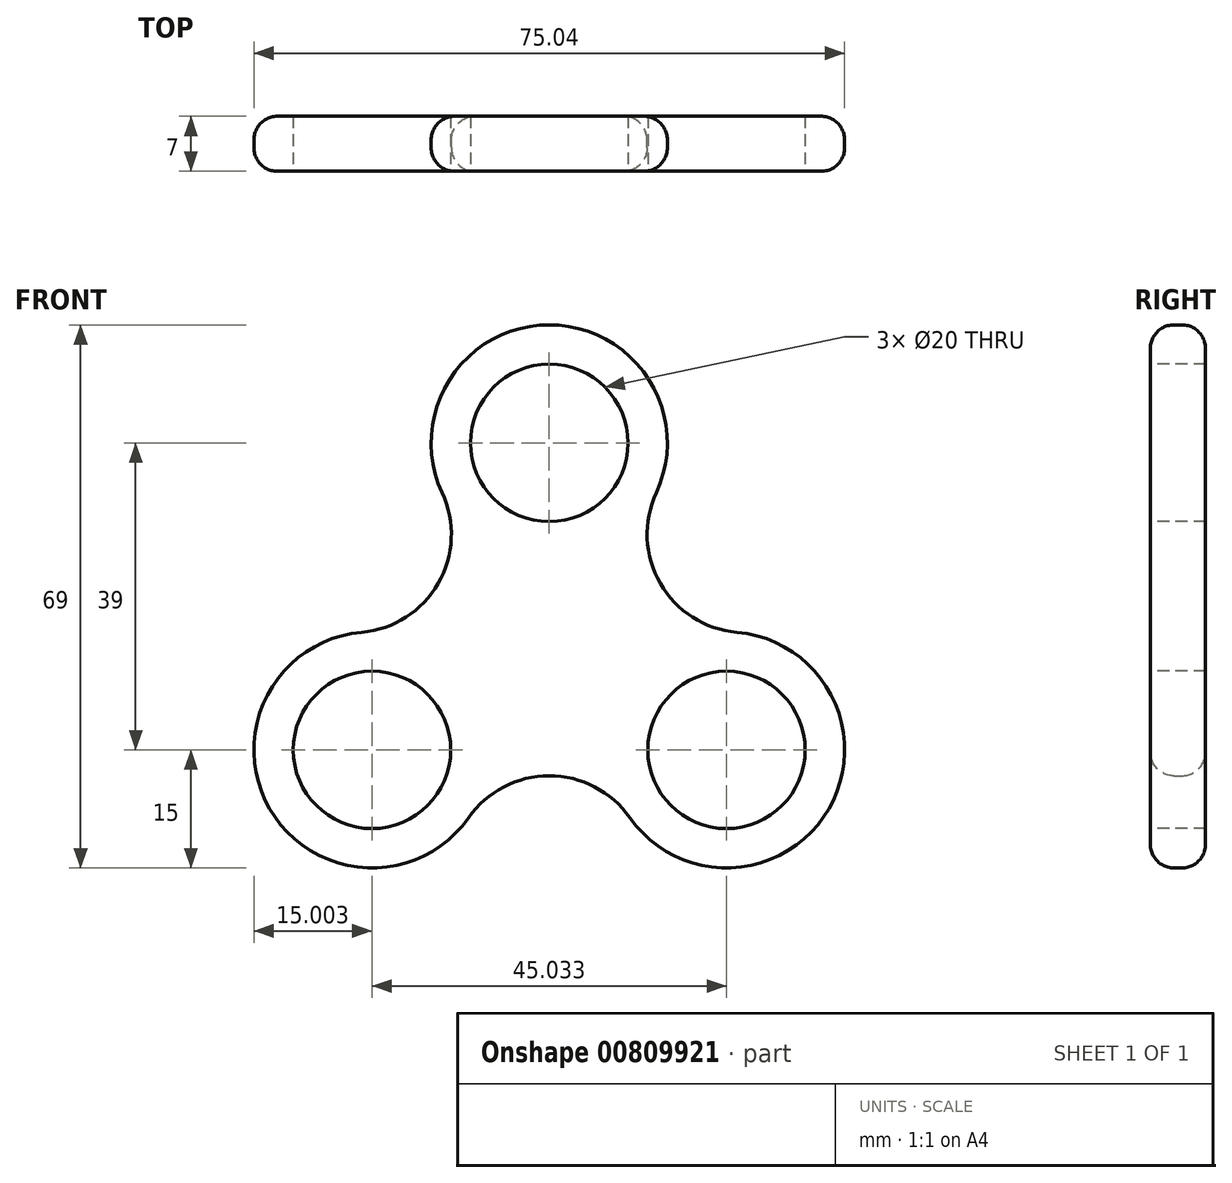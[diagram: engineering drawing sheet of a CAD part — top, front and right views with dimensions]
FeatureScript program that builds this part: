
annotation { "Feature Type Name" : "Feature", "Feature Type Description" : "" }
export const myFeature = defineFeature(function(context is Context, id is Id, definition is map)
    precondition{}
    {
        {
            var Q0;
            Q0=qCreatedBy(makeId("Front.planeOp"),FACE);
            var sketch = newSketch(context, id + "F0", { "sketchPlane" : qUnion([Q0])});
            skCircle(sketch, "E0", {"center": v(0, 26) * mm, "radius": 15 * mm});
            skCircle(sketch, "E1", {"center": v(-22.52, -13) * mm, "radius": 15 * mm});
            skCircle(sketch, "E2", {"center": v(22.52, -13) * mm, "radius": 15 * mm});
            skCircle(sketch, "E3", {"center": v(0, 0) * mm, "radius": 26 * mm, "construction": true});
            skLineSegment(sketch, "E4", {"start": v(0, 0) * mm, "end": v(-56.23, -32.46) * mm, "construction": true});
            skLineSegment(sketch, "E5", {"start": v(0, 0) * mm, "end": v(54.96, -31.73) * mm, "construction": true});
            skArc(sketch, "E6", {"start": v(-23.83, 1.94) * mm, "mid": v(-14.1, 8.14) * mm, "end": v(-13.6, 19.67) * mm});
            skArc(sketch, "E7", {"start": v(10.23, -21.61) * mm, "mid": v(0, -16.29) * mm, "end": v(-10.23, -21.61) * mm});
            skArc(sketch, "E8", {"start": v(13.6, 19.67) * mm, "mid": v(14.1, 8.14) * mm, "end": v(23.83, 1.94) * mm});
            skSolve(sketch);
        }
        {
            var Q0;
            {var subQ0=sQuery(id+"F0.wireOp",EDGE,"E0");var subQ1=makeQuery(id+"F0.imprint","INTERSECT",VERTEX,{"derivedFrom":[subQ0,sQuery(id+"F0.wireOp",EDGE,"E6")]});Q0=makeQuery(id+"F0.imprint","IMPRINT",FACE,{"disambiguationData":[TD([[makeQuery(id+"F0.imprint","IMPRINT",EDGE,{"disambiguationData":[TD([[subQ1,-1.0]])],"derivedFrom":subQ0}),1.0]])]});}
            var Q1;
            {var subQ0=sQuery(id+"F0.wireOp",EDGE,"E1");var subQ1=makeQuery(id+"F0.imprint","INTERSECT",VERTEX,{"derivedFrom":[subQ0,sQuery(id+"F0.wireOp",EDGE,"E6")]});Q1=makeQuery(id+"F0.imprint","IMPRINT",FACE,{"disambiguationData":[TD([[makeQuery(id+"F0.imprint","IMPRINT",EDGE,{"disambiguationData":[TD([[subQ1,-1.0]])],"derivedFrom":subQ0}),1.0]])]});}
            var Q2;
            {var subQ0=sQuery(id+"F0.wireOp",EDGE,"E2");var subQ1=makeQuery(id+"F0.imprint","INTERSECT",VERTEX,{"derivedFrom":[subQ0,sQuery(id+"F0.wireOp",EDGE,"E7")]});Q2=makeQuery(id+"F0.imprint","IMPRINT",FACE,{"disambiguationData":[TD([[makeQuery(id+"F0.imprint","IMPRINT",EDGE,{"disambiguationData":[TD([[subQ1,1.0]])],"derivedFrom":subQ0}),1.0]])]});}
            var Q3;
            {var subQ0=sQuery(id+"F0.wireOp",EDGE,"E6");Q3=makeQuery(id+"F0.imprint","IMPRINT",FACE,{"disambiguationData":[TD([[makeQuery(id+"F0.imprint","IMPRINT",EDGE,{"derivedFrom":subQ0}),-1.0]])]});}
            extrude(context, id + "F1", {"entities" : qUnion([Q0, Q1, Q2, Q3]), "depth" : 7 * mm, "offsetDistance" : 25 * mm, "symmetric" : true});
        }
        {
            var Q0;
            Q0=makeQuery(id+"F1.opExtrude","CAP_FACE",FACE,{"disambiguationData":[OSD([sQuery(id+"F0.wireOp",EDGE,"E0"),sQuery(id+"F0.wireOp",EDGE,"E1"),sQuery(id+"F0.wireOp",EDGE,"E2"),sQuery(id+"F0.wireOp",EDGE,"E6"),sQuery(id+"F0.wireOp",EDGE,"E7"),sQuery(id+"F0.wireOp",EDGE,"E8")])],"isStart":false});
            var Q1;
            Q1=makeQuery(id+"F1.opExtrude","CAP_FACE",FACE,{"disambiguationData":[OSD([sQuery(id+"F0.wireOp",EDGE,"E0"),sQuery(id+"F0.wireOp",EDGE,"E1"),sQuery(id+"F0.wireOp",EDGE,"E2"),sQuery(id+"F0.wireOp",EDGE,"E6"),sQuery(id+"F0.wireOp",EDGE,"E7"),sQuery(id+"F0.wireOp",EDGE,"E8")])],"isStart":true});
            fillet(context, id + "F2", {"entities" : qUnion([Q0, Q1]), "radius" : 3 * mm, "tangentPropagation" : true, "allowEdgeOverflow" : false});
        }
        {
            var Q0;
            Q0=makeQuery(id+"F1.opExtrude","CAP_FACE",FACE,{"disambiguationData":[OSD([sQuery(id+"F0.wireOp",EDGE,"E0"),sQuery(id+"F0.wireOp",EDGE,"E1"),sQuery(id+"F0.wireOp",EDGE,"E2"),sQuery(id+"F0.wireOp",EDGE,"E6"),sQuery(id+"F0.wireOp",EDGE,"E7"),sQuery(id+"F0.wireOp",EDGE,"E8")])],"isStart":false});
            var sketch = newSketch(context, id + "F3", { "sketchPlane" : qUnion([Q0])});
            skPoint(sketch, "E9", {"position": v(-22.52, -13) * mm});
            skPoint(sketch, "E10", {"position": v(0, 26) * mm});
            skPoint(sketch, "E11", {"position": v(22.52, -13) * mm});
            skSolve(sketch);
        }
        {
            var Q0;
            Q0=sQuery(id+"F3.wireOp",VERTEX,"E10");
            var Q1;
            Q1=sQuery(id+"F3.wireOp",VERTEX,"E9");
            var Q2;
            Q2=sQuery(id+"F3.wireOp",VERTEX,"E11");
            var Q3;
            Q3=makeQuery(id+"F1.opExtrude","SWEPT_BODY",BODY,{"disambiguationData":[OSD([sQuery(id+"F0.wireOp",EDGE,"E0"),sQuery(id+"F0.wireOp",EDGE,"E1"),sQuery(id+"F0.wireOp",EDGE,"E2"),sQuery(id+"F0.wireOp",EDGE,"E6"),sQuery(id+"F0.wireOp",EDGE,"E7"),sQuery(id+"F0.wireOp",EDGE,"E8")])]});
            hole(context, id + "F4", {"style" : HoleStyle.SIMPLE, "endStyle" : HoleEndStyle.THROUGH, "holeDiameter" : 20 * mm, "majorDiameter" : 5 * mm, "isTappedThrough" : true, "tappedDepth" : 12 * mm, "tapClearance" : 3, "locations" : qUnion([Q0, Q1, Q2]), "scope" : qUnion([Q3])});
        }
    });
